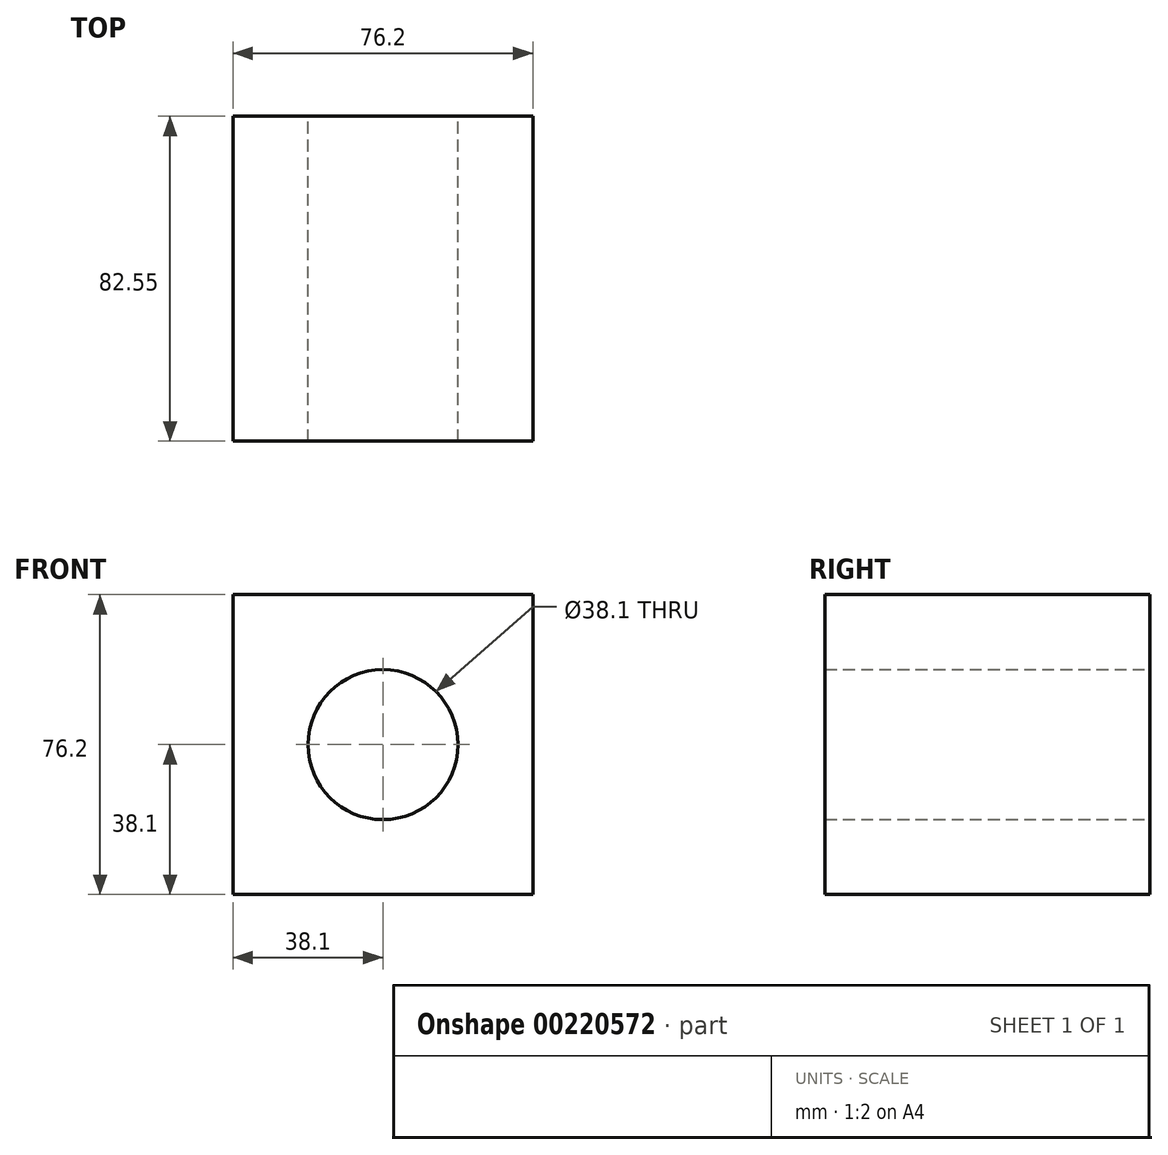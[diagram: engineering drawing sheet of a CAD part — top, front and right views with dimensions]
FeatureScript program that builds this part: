
annotation { "Feature Type Name" : "Feature", "Feature Type Description" : "" }
export const myFeature = defineFeature(function(context is Context, id is Id, definition is map)
    precondition{}
    {
        {
            var Q0;
            Q0=qCreatedBy(makeId("Front.planeOp"),FACE);
            var sketch = newSketch(context, id + "F0", { "sketchPlane" : qUnion([Q0])});
            skLineSegment(sketch, "E0.bottom", {"start": v(38.1, -38.1) * mm, "end": v(-38.1, -38.1) * mm});
            skLineSegment(sketch, "E0.top", {"start": v(38.1, 38.1) * mm, "end": v(-38.1, 38.1) * mm});
            skLineSegment(sketch, "E0.left", {"start": v(38.1, -38.1) * mm, "end": v(38.1, 38.1) * mm});
            skLineSegment(sketch, "E0.right", {"start": v(-38.1, -38.1) * mm, "end": v(-38.1, 38.1) * mm});
            skPoint(sketch, "E0.middle", {"position": v(0, 0) * mm});
            skCircle(sketch, "E1", {"center": v(0, 0) * mm, "radius": 19.05 * mm});
            skSolve(sketch);
        }
        {
            var Q0;
            Q0 = qSketchRegion(id + "F0", true);
            extrude(context, id + "F1", {"entities" : qUnion([Q0]), "depth" : 82.55 * mm});
        }
    });
